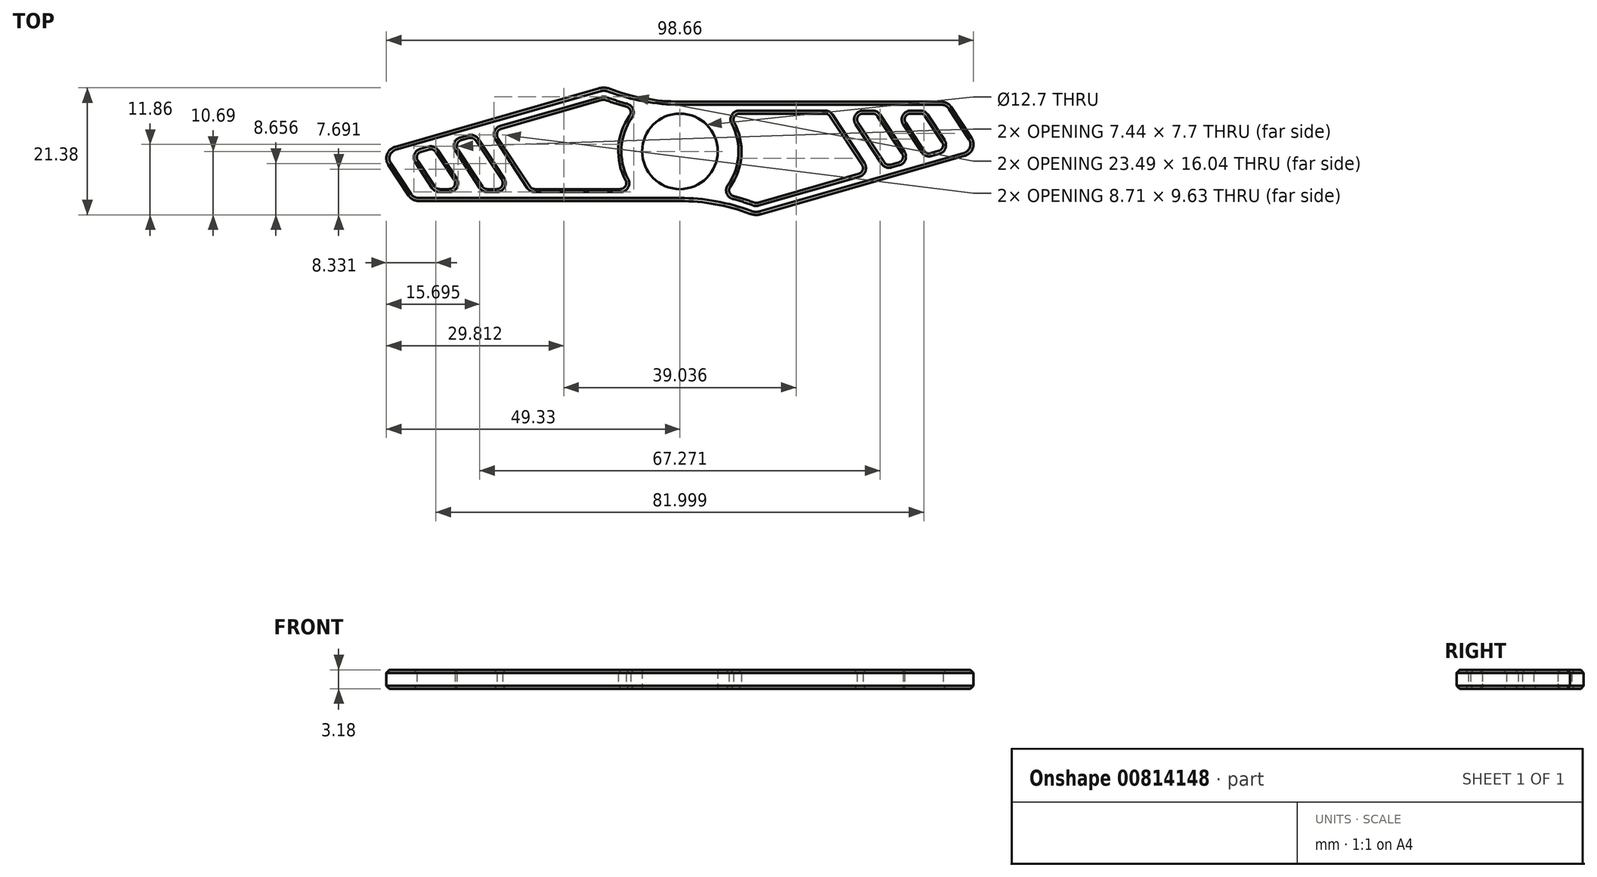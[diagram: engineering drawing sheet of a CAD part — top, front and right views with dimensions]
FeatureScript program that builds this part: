
annotation { "Feature Type Name" : "Feature", "Feature Type Description" : "" }
export const myFeature = defineFeature(function(context is Context, id is Id, definition is map)
    precondition{}
    {
        {
            var Q0;
            Q0=qCreatedBy(makeId("Top.planeOp"),FACE);
            var sketch = newSketch(context, id + "F0", { "sketchPlane" : qUnion([Q0])});
            skCircle(sketch, "E0", {"center": v(0, 0) * mm, "radius": 6.35 * mm});
            skLineSegment(sketch, "E1", {"start": v(0, 8.35) * mm, "end": v(43.92, 8.35) * mm});
            skLineSegment(sketch, "E2", {"start": v(45.6, 7.45) * mm, "end": v(49, 2.27) * mm});
            skLineSegment(sketch, "E3", {"start": v(0, 8.35) * mm, "end": v(12.66, -10.85) * mm, "construction": true});
            skArc(sketch, "E4", {"start": v(0, -8.35) * mm, "mid": v(5.97, -8.9) * mm, "end": v(11.75, -10.5) * mm});
            skLineSegment(sketch, "E5", {"start": v(13.64, -10.57) * mm, "end": v(47.89, -0.75) * mm});
            skCircle(sketch, "E6.0", {"center": v(0, 0) * mm, "radius": 10.35 * mm, "construction": true});
            skArc(sketch, "E7.0", {"start": v(0, -6.35) * mm, "mid": v(6.5, -6.95) * mm, "end": v(12.76, -8.74) * mm, "construction": true});
            skLineSegment(sketch, "E7.1", {"start": v(12.76, -8.74) * mm, "end": v(47.33, 1.17) * mm, "construction": true});
            skLineSegment(sketch, "E7.2", {"start": v(43.92, 6.35) * mm, "end": v(47.33, 1.17) * mm, "construction": true});
            skLineSegment(sketch, "E7.3", {"start": v(0, 6.35) * mm, "end": v(43.92, 6.35) * mm, "construction": true});
            skLineSegment(sketch, "E8", {"start": v(43.92, 6.35) * mm, "end": v(40.92, 6.35) * mm, "construction": true});
            skLineSegment(sketch, "E9", {"start": v(41.22, 5.9) * mm, "end": v(44.06, 1.58) * mm});
            skLineSegment(sketch, "E10", {"start": v(40.38, 6.35) * mm, "end": v(38.78, 6.35) * mm});
            skLineSegment(sketch, "E11", {"start": v(37.94, 4.8) * mm, "end": v(41.04, 0.1) * mm});
            skLineSegment(sketch, "E12", {"start": v(43.5, 0.07) * mm, "end": v(42.15, -0.31) * mm});
            skLineSegment(sketch, "E13", {"start": v(36.92, 6.35) * mm, "end": v(32.92, 6.35) * mm, "construction": true});
            skLineSegment(sketch, "E14", {"start": v(33.22, 5.9) * mm, "end": v(37.33, -0.35) * mm});
            skLineSegment(sketch, "E15", {"start": v(32.38, 6.35) * mm, "end": v(30.78, 6.35) * mm});
            skLineSegment(sketch, "E16", {"start": v(29.94, 4.8) * mm, "end": v(34.31, -1.83) * mm});
            skLineSegment(sketch, "E17", {"start": v(35.43, -2.24) * mm, "end": v(36.78, -1.86) * mm});
            skLineSegment(sketch, "E18", {"start": v(28.92, 6.35) * mm, "end": v(24.92, 6.35) * mm, "construction": true});
            skLineSegment(sketch, "E19", {"start": v(25.22, 5.9) * mm, "end": v(30.6, -2.27) * mm});
            skLineSegment(sketch, "E20", {"start": v(30.05, -3.79) * mm, "end": v(13.08, -8.65) * mm});
            skPoint(sketch, "E21", {"position": v(10.35, 0) * mm});
            skLineSegment(sketch, "E22", {"start": v(24.38, 6.35) * mm, "end": v(10, 6.35) * mm});
            skPoint(sketch, "E23", {"position": v(9.72, -7.72) * mm});
            skArc(sketch, "E24", {"start": v(12.45, -8.63) * mm, "mid": v(10.75, -8.03) * mm, "end": v(9, -7.52) * mm});
            skArc(sketch, "E25", {"start": v(8.45, -5.98) * mm, "mid": v(10.33, -0.65) * mm, "end": v(9.13, 4.88) * mm});
            skPoint(sketch, "E26.visualSharp", {"position": v(8.17, 6.35) * mm});
            skArc(sketch, "E26.filletArc", {"start": v(10, 6.35) * mm, "mid": v(9.15, 5.86) * mm, "end": v(9.13, 4.88) * mm});
            skPoint(sketch, "E27.visualSharp", {"position": v(24.92, 6.35) * mm});
            skArc(sketch, "E27.filletArc", {"start": v(25.22, 5.9) * mm, "mid": v(24.86, 6.23) * mm, "end": v(24.38, 6.35) * mm});
            skPoint(sketch, "E28.visualSharp", {"position": v(31.36, -3.41) * mm});
            skArc(sketch, "E28.filletArc", {"start": v(30.05, -3.79) * mm, "mid": v(30.7, -3.17) * mm, "end": v(30.6, -2.27) * mm});
            skPoint(sketch, "E29.visualSharp", {"position": v(12.76, -8.74) * mm});
            skArc(sketch, "E29.filletArc", {"start": v(12.45, -8.63) * mm, "mid": v(12.77, -8.69) * mm, "end": v(13.08, -8.65) * mm});
            skPoint(sketch, "E30.visualSharp", {"position": v(7.48, -7.15) * mm});
            skArc(sketch, "E30.filletArc", {"start": v(8.45, -5.98) * mm, "mid": v(8.33, -6.9) * mm, "end": v(9, -7.52) * mm});
            skPoint(sketch, "E31.visualSharp", {"position": v(28.92, 6.35) * mm});
            skArc(sketch, "E31.filletArc", {"start": v(30.78, 6.35) * mm, "mid": v(29.9, 5.82) * mm, "end": v(29.94, 4.8) * mm});
            skPoint(sketch, "E32.visualSharp", {"position": v(32.92, 6.35) * mm});
            skArc(sketch, "E32.filletArc", {"start": v(33.22, 5.9) * mm, "mid": v(32.86, 6.23) * mm, "end": v(32.38, 6.35) * mm});
            skPoint(sketch, "E33.visualSharp", {"position": v(38.08, -1.48) * mm});
            skArc(sketch, "E33.filletArc", {"start": v(36.78, -1.86) * mm, "mid": v(37.44, -1.24) * mm, "end": v(37.33, -0.35) * mm});
            skPoint(sketch, "E34.visualSharp", {"position": v(34.72, -2.45) * mm});
            skArc(sketch, "E34.filletArc", {"start": v(34.31, -1.83) * mm, "mid": v(34.8, -2.22) * mm, "end": v(35.43, -2.24) * mm});
            skPoint(sketch, "E35.visualSharp", {"position": v(36.92, 6.35) * mm});
            skArc(sketch, "E35.filletArc", {"start": v(38.78, 6.35) * mm, "mid": v(37.9, 5.82) * mm, "end": v(37.94, 4.8) * mm});
            skPoint(sketch, "E36.visualSharp", {"position": v(40.92, 6.35) * mm});
            skArc(sketch, "E36.filletArc", {"start": v(41.22, 5.9) * mm, "mid": v(40.86, 6.23) * mm, "end": v(40.38, 6.35) * mm});
            skPoint(sketch, "E37.visualSharp", {"position": v(44.81, 0.45) * mm});
            skArc(sketch, "E37.filletArc", {"start": v(43.5, 0.07) * mm, "mid": v(44.17, 0.69) * mm, "end": v(44.06, 1.58) * mm});
            skPoint(sketch, "E38.visualSharp", {"position": v(41.45, -0.52) * mm});
            skArc(sketch, "E38.filletArc", {"start": v(41.04, 0.1) * mm, "mid": v(41.53, -0.3) * mm, "end": v(42.15, -0.31) * mm});
            skPoint(sketch, "E39.visualSharp", {"position": v(45, 8.35) * mm});
            skArc(sketch, "E39.filletArc", {"start": v(45.6, 7.45) * mm, "mid": v(44.87, 8.11) * mm, "end": v(43.92, 8.35) * mm});
            skPoint(sketch, "E40.visualSharp", {"position": v(50.5, 0) * mm});
            skArc(sketch, "E40.filletArc", {"start": v(47.89, -0.75) * mm, "mid": v(49.21, 0.48) * mm, "end": v(49, 2.27) * mm});
            skPoint(sketch, "E41.visualSharp", {"position": v(12.66, -10.85) * mm});
            skArc(sketch, "E41.filletArc", {"start": v(11.75, -10.5) * mm, "mid": v(12.69, -10.69) * mm, "end": v(13.64, -10.57) * mm});
            skLineSegment(sketch, "E42.1.0", {"start": v(-33.22, -5.9) * mm, "end": v(-37.33, 0.35) * mm});
            skArc(sketch, "E42.1.1", {"start": v(-30.78, -6.35) * mm, "mid": v(-29.9, -5.82) * mm, "end": v(-29.94, -4.8) * mm});
            skLineSegment(sketch, "E42.1.2", {"start": v(-36.92, -6.35) * mm, "end": v(-32.92, -6.35) * mm, "construction": true});
            skPoint(sketch, "E42.1.3", {"position": v(-12.76, 8.74) * mm});
            skPoint(sketch, "E42.1.4", {"position": v(-44.81, -0.45) * mm});
            skArc(sketch, "E42.1.5", {"start": v(-8.45, 5.98) * mm, "mid": v(-8.33, 6.9) * mm, "end": v(-9, 7.52) * mm});
            skLineSegment(sketch, "E42.1.6", {"start": v(-43.92, -6.35) * mm, "end": v(-40.92, -6.35) * mm, "construction": true});
            skLineSegment(sketch, "E42.1.7", {"start": v(-43.92, -6.35) * mm, "end": v(-47.33, -1.17) * mm, "construction": true});
            skLineSegment(sketch, "E42.1.8", {"start": v(-12.76, 8.74) * mm, "end": v(-47.33, -1.17) * mm, "construction": true});
            skLineSegment(sketch, "E42.1.9", {"start": v(-13.64, 10.57) * mm, "end": v(-47.89, 0.75) * mm});
            skLineSegment(sketch, "E42.1.10", {"start": v(-45.6, -7.45) * mm, "end": v(-49, -2.27) * mm});
            skLineSegment(sketch, "E42.1.11", {"start": v(-37.94, -4.8) * mm, "end": v(-41.04, -0.1) * mm});
            skLineSegment(sketch, "E42.1.12", {"start": v(-40.38, -6.35) * mm, "end": v(-38.78, -6.35) * mm});
            skLineSegment(sketch, "E42.1.13", {"start": v(-41.22, -5.9) * mm, "end": v(-44.06, -1.58) * mm});
            skPoint(sketch, "E42.1.14", {"position": v(-31.36, 3.41) * mm});
            skPoint(sketch, "E42.1.15", {"position": v(-40.92, -6.35) * mm});
            skArc(sketch, "E42.1.16", {"start": v(-30.05, 3.79) * mm, "mid": v(-30.7, 3.17) * mm, "end": v(-30.6, 2.27) * mm});
            skArc(sketch, "E42.1.17", {"start": v(-10, -6.35) * mm, "mid": v(-9.15, -5.86) * mm, "end": v(-9.13, -4.88) * mm});
            skPoint(sketch, "E42.1.18", {"position": v(-8.17, -6.35) * mm});
            skPoint(sketch, "E42.1.19", {"position": v(-34.72, 2.45) * mm});
            skArc(sketch, "E42.1.20", {"start": v(-8.45, 5.98) * mm, "mid": v(-10.33, 0.65) * mm, "end": v(-9.13, -4.88) * mm});
            skPoint(sketch, "E42.1.21", {"position": v(-24.92, -6.35) * mm});
            skPoint(sketch, "E42.1.22", {"position": v(-36.92, -6.35) * mm});
            skArc(sketch, "E42.1.23", {"start": v(-12.45, 8.63) * mm, "mid": v(-10.75, 8.03) * mm, "end": v(-9, 7.52) * mm});
            skArc(sketch, "E42.1.24", {"start": v(-47.89, 0.75) * mm, "mid": v(-49.21, -0.48) * mm, "end": v(-49, -2.27) * mm});
            skPoint(sketch, "E42.1.25", {"position": v(-12.66, 10.85) * mm});
            skPoint(sketch, "E42.1.26", {"position": v(-38.08, 1.48) * mm});
            skLineSegment(sketch, "E42.1.27", {"start": v(-24.38, -6.35) * mm, "end": v(-10, -6.35) * mm});
            skPoint(sketch, "E42.1.28", {"position": v(-9.72, 7.72) * mm});
            skPoint(sketch, "E42.1.29", {"position": v(-10.35, 0) * mm});
            skPoint(sketch, "E42.1.30", {"position": v(-32.92, -6.35) * mm});
            skLineSegment(sketch, "E42.1.31", {"start": v(-25.22, -5.9) * mm, "end": v(-30.6, 2.27) * mm});
            skArc(sketch, "E42.1.32", {"start": v(-43.5, -0.07) * mm, "mid": v(-44.17, -0.69) * mm, "end": v(-44.06, -1.58) * mm});
            skPoint(sketch, "E42.1.33", {"position": v(-50.5, 0) * mm});
            skLineSegment(sketch, "E42.1.34", {"start": v(-28.92, -6.35) * mm, "end": v(-24.92, -6.35) * mm, "construction": true});
            skArc(sketch, "E42.1.35", {"start": v(-38.78, -6.35) * mm, "mid": v(-37.9, -5.82) * mm, "end": v(-37.94, -4.8) * mm});
            skPoint(sketch, "E42.1.36", {"position": v(-28.92, -6.35) * mm});
            skPoint(sketch, "E42.1.37", {"position": v(-45, -8.35) * mm});
            skLineSegment(sketch, "E42.1.38", {"start": v(-29.94, -4.8) * mm, "end": v(-34.31, 1.83) * mm});
            skArc(sketch, "E42.1.39", {"start": v(-36.78, 1.86) * mm, "mid": v(-37.44, 1.24) * mm, "end": v(-37.33, 0.35) * mm});
            skLineSegment(sketch, "E42.1.40", {"start": v(-32.38, -6.35) * mm, "end": v(-30.78, -6.35) * mm});
            skPoint(sketch, "E42.1.41", {"position": v(-7.48, 7.15) * mm});
            skPoint(sketch, "E42.1.42", {"position": v(-41.45, 0.52) * mm});
            skLineSegment(sketch, "E42.1.43", {"start": v(-43.5, -0.07) * mm, "end": v(-42.15, 0.31) * mm});
            skArc(sketch, "E42.1.44", {"start": v(-45.6, -7.45) * mm, "mid": v(-44.87, -8.11) * mm, "end": v(-43.92, -8.35) * mm});
            skLineSegment(sketch, "E42.1.45", {"start": v(-30.05, 3.79) * mm, "end": v(-13.08, 8.65) * mm});
            skArc(sketch, "E42.1.46", {"start": v(-41.04, -0.1) * mm, "mid": v(-41.53, 0.3) * mm, "end": v(-42.15, 0.31) * mm});
            skLineSegment(sketch, "E42.1.47", {"start": v(-35.43, 2.24) * mm, "end": v(-36.78, 1.86) * mm});
            skArc(sketch, "E42.1.48", {"start": v(-34.31, 1.83) * mm, "mid": v(-34.8, 2.22) * mm, "end": v(-35.43, 2.24) * mm});
            skArc(sketch, "E42.1.49", {"start": v(-33.22, -5.9) * mm, "mid": v(-32.86, -6.23) * mm, "end": v(-32.38, -6.35) * mm});
            skArc(sketch, "E42.1.50", {"start": v(-25.22, -5.9) * mm, "mid": v(-24.86, -6.23) * mm, "end": v(-24.38, -6.35) * mm});
            skArc(sketch, "E42.1.51", {"start": v(-11.75, 10.5) * mm, "mid": v(-12.69, 10.69) * mm, "end": v(-13.64, 10.57) * mm});
            skArc(sketch, "E42.1.52", {"start": v(-41.22, -5.9) * mm, "mid": v(-40.86, -6.23) * mm, "end": v(-40.38, -6.35) * mm});
            skArc(sketch, "E42.1.53", {"start": v(-12.45, 8.63) * mm, "mid": v(-12.77, 8.69) * mm, "end": v(-13.08, 8.65) * mm});
            skLineSegment(sketch, "E42.1.54", {"start": v(0, -8.35) * mm, "end": v(-43.92, -8.35) * mm});
            skArc(sketch, "E42.1.55", {"start": v(0, 8.35) * mm, "mid": v(-5.97, 8.9) * mm, "end": v(-11.75, 10.5) * mm});
            skSolve(sketch);
        }
        {
            var Q0;
            Q0=makeQuery(id+"F0.imprint","IMPRINT",FACE,{"disambiguationData":[TD([[makeQuery(id+"F0.imprint","IMPRINT",EDGE,{"derivedFrom":sQuery(id+"F0.wireOp",EDGE,"E0")}),-1.0]])]});
            extrude(context, id + "F1", {"entities" : qUnion([Q0]), "depth" : 3.17 * mm, "offsetDistance" : 25 * mm});
        }
        {
            var Q0;
            Q0=makeQuery(id+"F1.opExtrude","CAP_EDGE",EDGE,{"disambiguationData":[OSD([sQuery(id+"F0.wireOp",EDGE,"E1")])],"isStart":true});
            var Q1;
            Q1=makeQuery(id+"F1.opExtrude","CAP_EDGE",EDGE,{"disambiguationData":[OSD([sQuery(id+"F0.wireOp",EDGE,"E42.1.54")])],"isStart":false});
            var Q2;
            Q2=makeQuery(id+"F1.opExtrude","CAP_EDGE",EDGE,{"disambiguationData":[OSD([sQuery(id+"F0.wireOp",EDGE,"E42.1.45")])],"isStart":false});
            var Q3;
            Q3=makeQuery(id+"F1.opExtrude","CAP_EDGE",EDGE,{"disambiguationData":[OSD([sQuery(id+"F0.wireOp",EDGE,"E42.1.38")])],"isStart":false});
            var Q4;
            Q4=makeQuery(id+"F1.opExtrude","CAP_EDGE",EDGE,{"disambiguationData":[OSD([sQuery(id+"F0.wireOp",EDGE,"E42.1.11")])],"isStart":false});
            var Q5;
            Q5=makeQuery(id+"F1.opExtrude","CAP_EDGE",EDGE,{"disambiguationData":[OSD([sQuery(id+"F0.wireOp",EDGE,"E22")])],"isStart":false});
            var Q6;
            Q6=makeQuery(id+"F1.opExtrude","CAP_EDGE",EDGE,{"disambiguationData":[OSD([sQuery(id+"F0.wireOp",EDGE,"E16")])],"isStart":false});
            var Q7;
            Q7=makeQuery(id+"F1.opExtrude","CAP_EDGE",EDGE,{"disambiguationData":[OSD([sQuery(id+"F0.wireOp",EDGE,"E11")])],"isStart":false});
            var Q8;
            Q8=makeQuery(id+"F1.opExtrude","CAP_EDGE",EDGE,{"disambiguationData":[OSD([sQuery(id+"F0.wireOp",EDGE,"E9")])],"isStart":true});
            var Q9;
            Q9=makeQuery(id+"F1.opExtrude","CAP_EDGE",EDGE,{"disambiguationData":[OSD([sQuery(id+"F0.wireOp",EDGE,"E14")])],"isStart":true});
            var Q10;
            Q10=makeQuery(id+"F1.opExtrude","CAP_EDGE",EDGE,{"disambiguationData":[OSD([sQuery(id+"F0.wireOp",EDGE,"E22")])],"isStart":true});
            var Q11;
            Q11=makeQuery(id+"F1.opExtrude","CAP_EDGE",EDGE,{"disambiguationData":[OSD([sQuery(id+"F0.wireOp",EDGE,"E42.1.45")])],"isStart":true});
            var Q12;
            Q12=makeQuery(id+"F1.opExtrude","CAP_EDGE",EDGE,{"disambiguationData":[OSD([sQuery(id+"F0.wireOp",EDGE,"E42.1.1")])],"isStart":true});
            var Q13;
            Q13=makeQuery(id+"F1.opExtrude","CAP_EDGE",EDGE,{"disambiguationData":[OSD([sQuery(id+"F0.wireOp",EDGE,"E42.1.35")])],"isStart":true});
            chamfer(context, id + "F2", {"entities" : qUnion([Q0, Q1, Q2, Q3, Q4, Q5, Q6, Q7, Q8, Q9, Q10, Q11, Q12, Q13]), "width" : 0.5 * mm, "tangentPropagation" : true});
        }
    });
